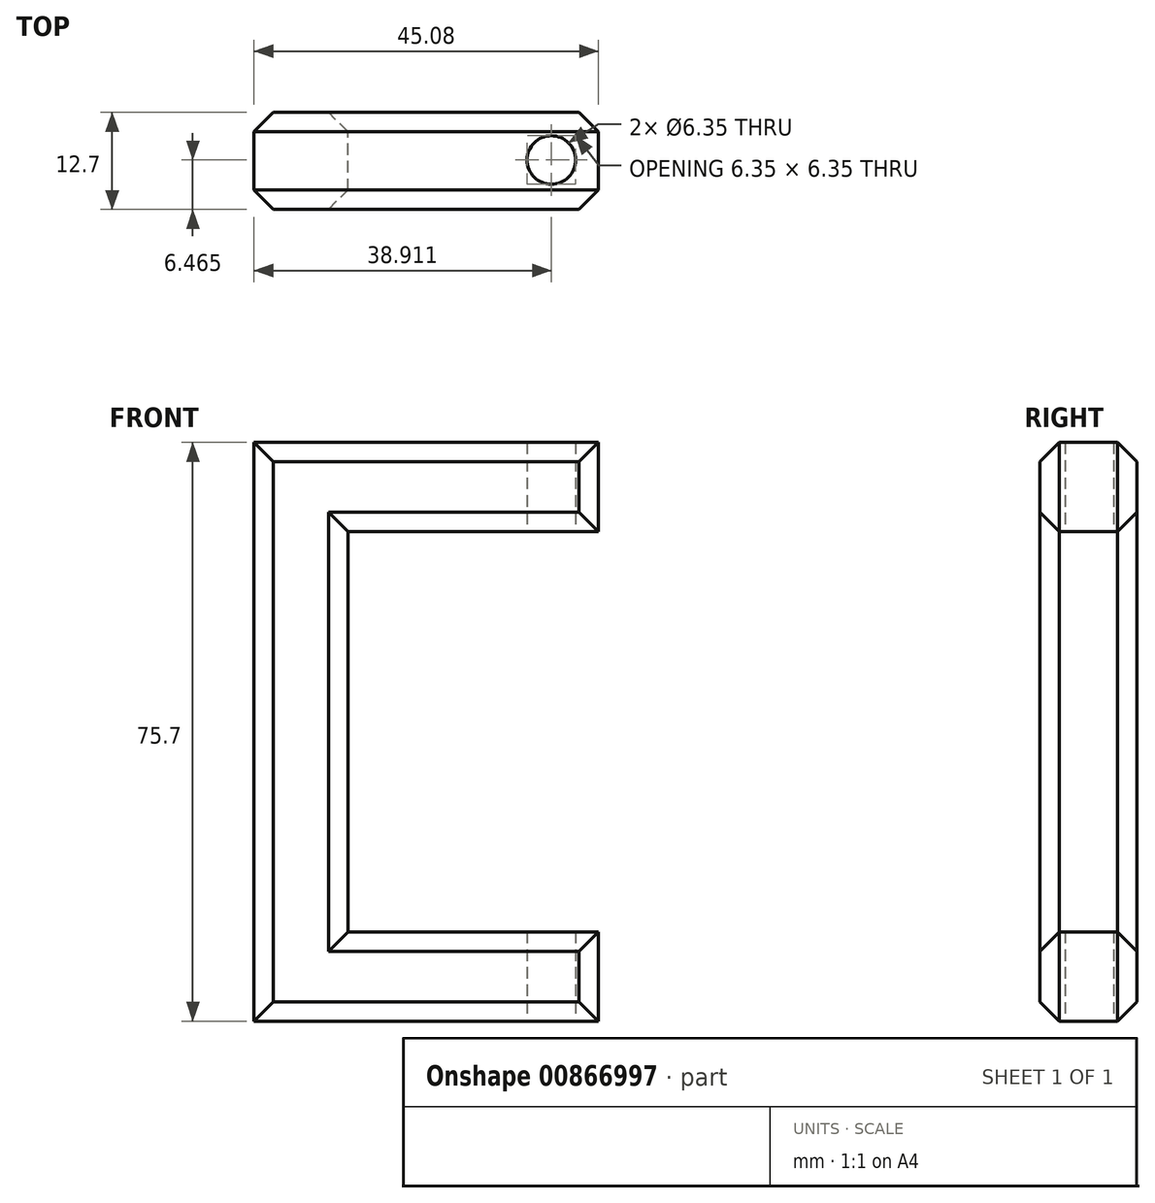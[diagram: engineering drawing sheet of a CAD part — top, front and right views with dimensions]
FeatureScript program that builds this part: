
annotation { "Feature Type Name" : "Feature", "Feature Type Description" : "" }
export const myFeature = defineFeature(function(context is Context, id is Id, definition is map)
    precondition{}
    {
        {
            var Q0;
            Q0=qCreatedBy(makeId("Front.planeOp"),FACE);
            var sketch = newSketch(context, id + "F0", { "sketchPlane" : qUnion([Q0])});
            skLineSegment(sketch, "E0", {"start": v(0, 0) * mm, "end": v(-45.08, 0) * mm});
            skLineSegment(sketch, "E1", {"start": v(-45.08, 0) * mm, "end": v(-45.08, 75.7) * mm});
            skLineSegment(sketch, "E2", {"start": v(-45.08, 75.7) * mm, "end": v(0, 75.7) * mm});
            skLineSegment(sketch, "E3", {"start": v(0, 75.7) * mm, "end": v(0, 64.02) * mm});
            skLineSegment(sketch, "E4", {"start": v(0, 64.02) * mm, "end": v(-32.8, 64.02) * mm});
            skLineSegment(sketch, "E5", {"start": v(-32.8, 64.02) * mm, "end": v(-32.8, 11.67) * mm});
            skLineSegment(sketch, "E6", {"start": v(-32.8, 11.67) * mm, "end": v(0, 11.67) * mm});
            skLineSegment(sketch, "E7", {"start": v(0, 11.67) * mm, "end": v(0, 0) * mm});
            skSolve(sketch);
        }
        {
            var Q0;
            Q0=makeQuery(id+"F0.imprint","IMPRINT",FACE,{"disambiguationData":[TD([[makeQuery(id+"F0.imprint","IMPRINT",EDGE,{"derivedFrom":sQuery(id+"F0.wireOp",EDGE,"E0")}),-1.0]])]});
            extrude(context, id + "F1", {"entities" : qUnion([Q0]), "endBound" : BoundingType.SYMMETRIC, "depth" : 12.7 * mm, "offsetDistance" : 25.4 * mm});
        }
        {
            var Q0;
            Q0=qCreatedBy(makeId("Top.planeOp"),FACE);
            var sketch = newSketch(context, id + "F2", { "sketchPlane" : qUnion([Q0])});
            skCircle(sketch, "E8", {"center": v(-6.17, 0.11) * mm, "radius": 6.17 * mm});
            skPoint(sketch, "E8.first.point", {"position": v(0, 0) * mm});
            skPoint(sketch, "E8.second.point", {"position": v(-12.34, 0) * mm});
            skPoint(sketch, "E8.third.point", {"position": v(-6.75, -6.03) * mm});
            skSolve(sketch);
        }
        {
            var Q0;
            Q0=sQuery(id+"F2.wireOp",VERTEX,"E8.center");
            var Q1;
            Q1=makeQuery(id+"F1.opExtrude","SWEPT_BODY",BODY,{"disambiguationData":[OSD([sQuery(id+"F0.wireOp",EDGE,"E0"),sQuery(id+"F0.wireOp",EDGE,"E1"),sQuery(id+"F0.wireOp",EDGE,"E2"),sQuery(id+"F0.wireOp",EDGE,"E3"),sQuery(id+"F0.wireOp",EDGE,"E4"),sQuery(id+"F0.wireOp",EDGE,"E5"),sQuery(id+"F0.wireOp",EDGE,"E6"),sQuery(id+"F0.wireOp",EDGE,"E7")])]});
            hole(context, id + "F3", {"style" : HoleStyle.SIMPLE, "endStyle" : HoleEndStyle.THROUGH, "oppositeDirection" : true, "holeDiameter" : 6.35 * mm, "majorDiameter" : 6.35 * mm, "isTappedThrough" : true, "tappedDepth" : 12.7 * mm, "tapClearance" : 3, "locations" : qUnion([Q0]), "scope" : qUnion([Q1])});
        }
        {
            var Q0;
            Q0=makeQuery(id+"F1.opExtrude","CAP_EDGE",EDGE,{"disambiguationData":[OSD([sQuery(id+"F0.wireOp",EDGE,"E2")])],"isStart":false});
            var Q1;
            Q1=makeQuery(id+"F1.opExtrude","CAP_EDGE",EDGE,{"disambiguationData":[OSD([sQuery(id+"F0.wireOp",EDGE,"E2")])],"isStart":true});
            var Q2;
            Q2=makeQuery(id+"F1.opExtrude","CAP_EDGE",EDGE,{"disambiguationData":[OSD([sQuery(id+"F0.wireOp",EDGE,"E4")])],"isStart":false});
            var Q3;
            Q3=makeQuery(id+"F1.opExtrude","CAP_EDGE",EDGE,{"disambiguationData":[OSD([sQuery(id+"F0.wireOp",EDGE,"E3")])],"isStart":false});
            var Q4;
            Q4=makeQuery(id+"F1.opExtrude","CAP_EDGE",EDGE,{"disambiguationData":[OSD([sQuery(id+"F0.wireOp",EDGE,"E3")])],"isStart":true});
            var Q5;
            Q5=makeQuery(id+"F1.opExtrude","CAP_EDGE",EDGE,{"disambiguationData":[OSD([sQuery(id+"F0.wireOp",EDGE,"E4")])],"isStart":true});
            chamfer(context, id + "F4", {"entities" : qUnion([Q0, Q1, Q2, Q3, Q4, Q5]), "width" : 2.54 * mm, "tangentPropagation" : true});
        }
        {
            var Q0;
            Q0=makeQuery(id+"F1.opExtrude","CAP_EDGE",EDGE,{"disambiguationData":[OSD([sQuery(id+"F0.wireOp",EDGE,"E0")])],"isStart":true});
            var Q1;
            Q1=makeQuery(id+"F1.opExtrude","CAP_EDGE",EDGE,{"disambiguationData":[OSD([sQuery(id+"F0.wireOp",EDGE,"E7")])],"isStart":false});
            var Q2;
            Q2=makeQuery(id+"F1.opExtrude","CAP_EDGE",EDGE,{"disambiguationData":[OSD([sQuery(id+"F0.wireOp",EDGE,"E0")])],"isStart":false});
            var Q3;
            Q3=makeQuery(id+"F1.opExtrude","CAP_EDGE",EDGE,{"disambiguationData":[OSD([sQuery(id+"F0.wireOp",EDGE,"E6")])],"isStart":false});
            var Q4;
            Q4=makeQuery(id+"F1.opExtrude","CAP_EDGE",EDGE,{"disambiguationData":[OSD([sQuery(id+"F0.wireOp",EDGE,"E7")])],"isStart":true});
            var Q5;
            Q5=makeQuery(id+"F1.opExtrude","CAP_EDGE",EDGE,{"disambiguationData":[OSD([sQuery(id+"F0.wireOp",EDGE,"E6")])],"isStart":true});
            chamfer(context, id + "F5", {"entities" : qUnion([Q0, Q1, Q2, Q3, Q4, Q5]), "width" : 2.54 * mm, "tangentPropagation" : true});
        }
        {
            var Q0;
            Q0=makeQuery(id+"F1.opExtrude","CAP_EDGE",EDGE,{"disambiguationData":[OSD([sQuery(id+"F0.wireOp",EDGE,"E1")])],"isStart":true});
            var Q1;
            Q1=makeQuery(id+"F1.opExtrude","CAP_EDGE",EDGE,{"disambiguationData":[OSD([sQuery(id+"F0.wireOp",EDGE,"E5")])],"isStart":false});
            var Q2;
            Q2=makeQuery(id+"F1.opExtrude","CAP_EDGE",EDGE,{"disambiguationData":[OSD([sQuery(id+"F0.wireOp",EDGE,"E5")])],"isStart":true});
            var Q3;
            Q3=makeQuery(id+"F1.opExtrude","CAP_EDGE",EDGE,{"disambiguationData":[OSD([sQuery(id+"F0.wireOp",EDGE,"E1")])],"isStart":false});
            chamfer(context, id + "F6", {"entities" : qUnion([Q0, Q1, Q2, Q3]), "width" : 2.54 * mm, "tangentPropagation" : true});
        }
    });
